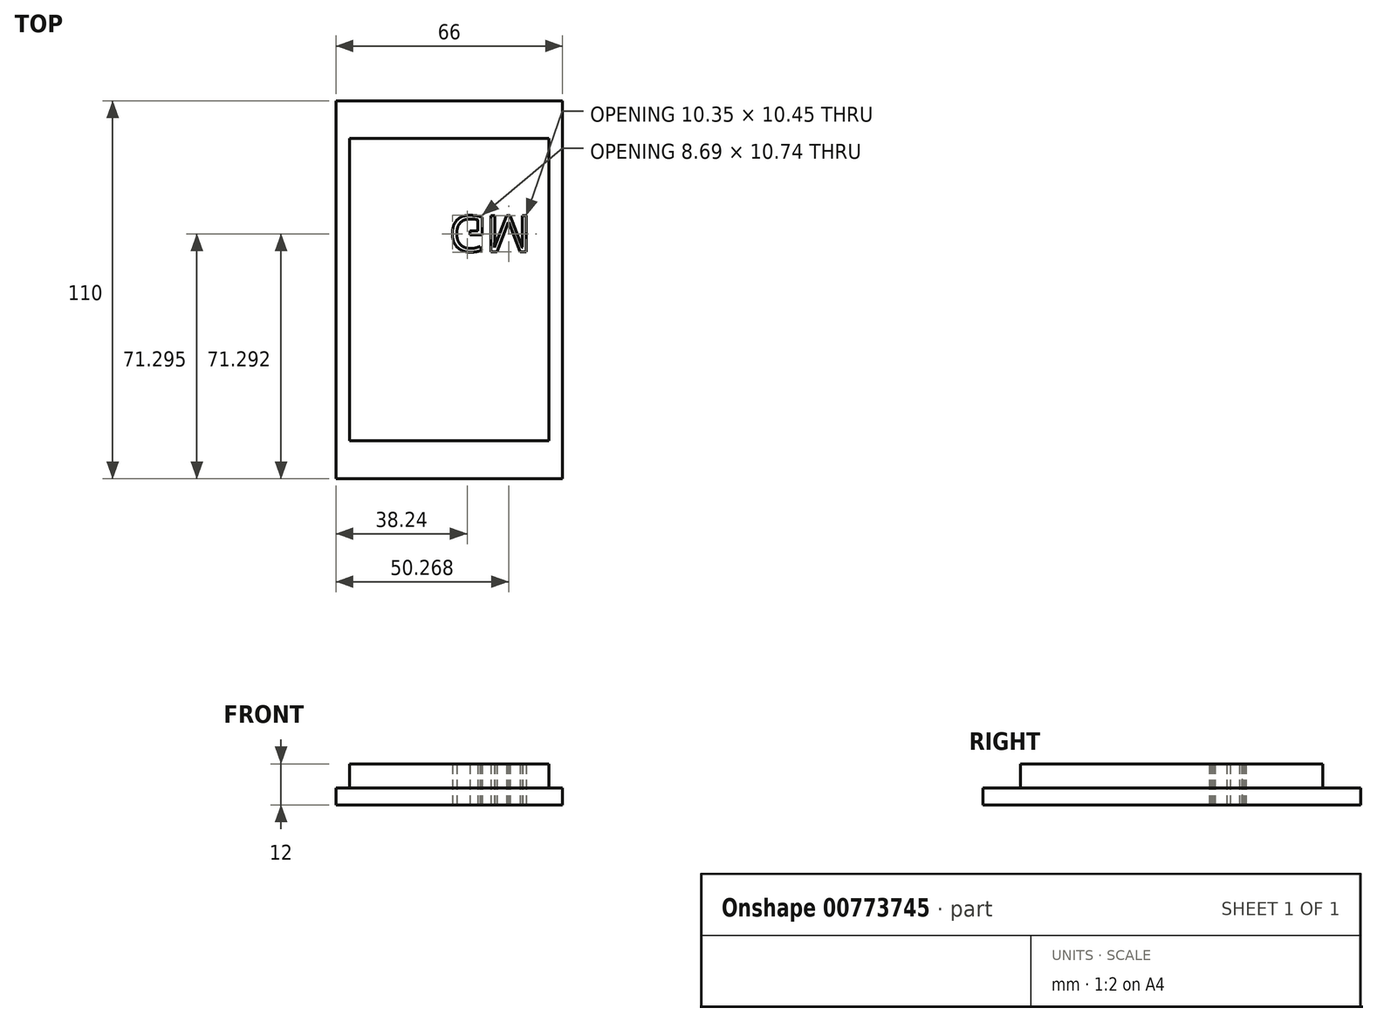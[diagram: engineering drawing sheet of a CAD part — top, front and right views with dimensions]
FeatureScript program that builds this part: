
annotation { "Feature Type Name" : "Feature", "Feature Type Description" : "" }
export const myFeature = defineFeature(function(context is Context, id is Id, definition is map)
    precondition{}
    {
        {
            var Q0;
            Q0=qCreatedBy(makeId("Top.planeOp"),FACE);
            var sketch = newSketch(context, id + "F0", { "sketchPlane" : qUnion([Q0])});
            skLineSegment(sketch, "E0.bottom", {"start": v(-33, 55) * mm, "end": v(33, 55) * mm});
            skLineSegment(sketch, "E0.top", {"start": v(-33, -55) * mm, "end": v(33, -55) * mm});
            skLineSegment(sketch, "E0.left", {"start": v(-33, 55) * mm, "end": v(-33, -55) * mm});
            skLineSegment(sketch, "E0.right", {"start": v(33, 55) * mm, "end": v(33, -55) * mm});
            skPoint(sketch, "E0.middle", {"position": v(0, 0) * mm});
            skSolve(sketch);
        }
        {
            var Q0;
            Q0=makeQuery(id+"F0.imprint","IMPRINT",FACE,{"disambiguationData":[TD([[makeQuery(id+"F0.imprint","IMPRINT",EDGE,{"derivedFrom":sQuery(id+"F0.wireOp",EDGE,"E0.bottom")}),-1.0]])]});
            extrude(context, id + "F1", {"entities" : qUnion([Q0]), "depth" : 5 * mm, "offsetDistance" : 25 * mm});
        }
        {
            var Q0;
            Q0=makeQuery(id+"F1.opExtrude","CAP_FACE",FACE,{"disambiguationData":[OSD([sQuery(id+"F0.wireOp",EDGE,"E0.bottom"),sQuery(id+"F0.wireOp",EDGE,"E0.top"),sQuery(id+"F0.wireOp",EDGE,"E0.left"),sQuery(id+"F0.wireOp",EDGE,"E0.right")])],"isStart":false});
            var sketch = newSketch(context, id + "F2", { "sketchPlane" : qUnion([Q0])});
            skLineSegment(sketch, "E1.bottom", {"start": v(-29, 44) * mm, "end": v(29, 44) * mm});
            skLineSegment(sketch, "E1.top", {"start": v(-29, -44) * mm, "end": v(29, -44) * mm});
            skLineSegment(sketch, "E1.left", {"start": v(-29, 44) * mm, "end": v(-29, -44) * mm});
            skLineSegment(sketch, "E1.right", {"start": v(29, 44) * mm, "end": v(29, -44) * mm});
            skPoint(sketch, "E1.middle", {"position": v(0, 0) * mm});
            skSolve(sketch);
        }
        {
            var Q0;
            Q0=makeQuery(id+"F2.imprint","IMPRINT",FACE,{"disambiguationData":[TD([[makeQuery(id+"F2.imprint","IMPRINT",EDGE,{"derivedFrom":sQuery(id+"F2.wireOp",EDGE,"E1.bottom")}),-1.0]])]});
            extrude(context, id + "F3", {"entities" : qUnion([Q0]), "operationType" : NewBodyOperationType.ADD, "depth" : 7 * mm, "offsetDistance" : 25 * mm});
        }
        {
            var Q0;
            Q0=makeQuery(id+"F1.opExtrude","CAP_FACE",FACE,{"disambiguationData":[OSD([sQuery(id+"F0.wireOp",EDGE,"E0.bottom"),sQuery(id+"F0.wireOp",EDGE,"E0.top"),sQuery(id+"F0.wireOp",EDGE,"E0.left"),sQuery(id+"F0.wireOp",EDGE,"E0.right")])],"isStart":true});
            var sketch = newSketch(context, id + "F4", { "sketchPlane" : qUnion([Q0])});
            skText(sketch, "E2", { "text": "GM\n", "fontName": "OpenSans-Regular.ttf"});
            const initialGuessF4  = {"E2": [0, -0.02152, 1, 0, 0.01054]};
            skSetInitialGuess(sketch, initialGuessF4);
            skSolve(sketch);
        }
        {
            var Q0;
            Q0 = qSketchRegion(id + "F4", true);
            extrude(context, id + "F5", {"entities" : qUnion([Q0]), "operationType" : NewBodyOperationType.REMOVE, "oppositeDirection" : true, "depth" : 38.7 * mm, "offsetDistance" : 25 * mm});
        }
    });
